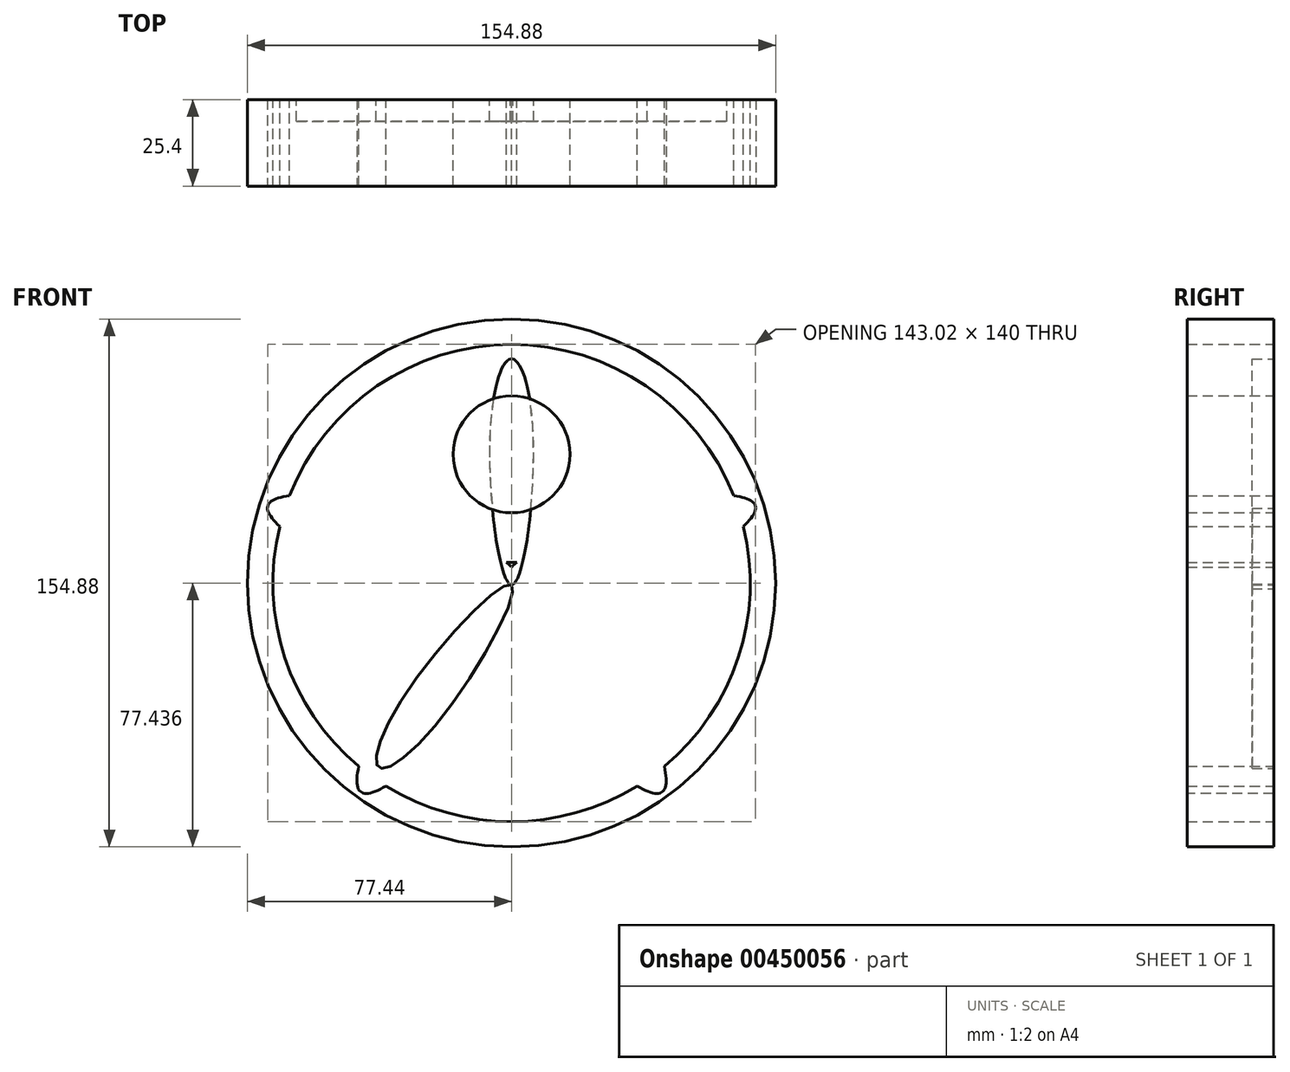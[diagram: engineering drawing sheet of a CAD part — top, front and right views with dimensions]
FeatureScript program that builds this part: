
annotation { "Feature Type Name" : "Feature", "Feature Type Description" : "" }
export const myFeature = defineFeature(function(context is Context, id is Id, definition is map)
    precondition{}
    {
        {
            var Q0;
            Q0=qCreatedBy(makeId("Front.planeOp"),FACE);
            var sketch = newSketch(context, id + "F0", { "sketchPlane" : qUnion([Q0])});
            skCircle(sketch, "E0", {"center": v(0, 0) * mm, "radius": 66.3 * mm, "construction": true});
            skLineSegment(sketch, "E1", {"start": v(0, 0) * mm, "end": v(-63.06, 20.49) * mm, "construction": true});
            skLineSegment(sketch, "E2", {"start": v(-38.97, -53.64) * mm, "end": v(0, 0) * mm, "construction": true});
            skLineSegment(sketch, "E3", {"start": v(0, 0) * mm, "end": v(38.97, -53.64) * mm, "construction": true});
            skLineSegment(sketch, "E4", {"start": v(38.97, -53.64) * mm, "end": v(0, 0) * mm, "construction": true});
            skLineSegment(sketch, "E5", {"start": v(63.06, 20.49) * mm, "end": v(0, 0) * mm, "construction": true});
            skFitSpline(sketch, "E6", {"points": [v(0, 0) * mm, v(-40.37, 19.8) * mm, v(-63.06, 20.49) * mm, v(-44.3, 7.71) * mm, v(0, 0) * mm]});
            skLineSegment(sketch, "E7", {"start": v(-40.37, 19.8) * mm, "end": v(-44.3, 7.71) * mm, "construction": true});
            skSolve(sketch);
        }
        {
            var Q0;
            Q0 = qSketchRegion(id + "F0", true);
            extrude(context, id + "F1", {"entities" : qUnion([Q0]), "depth" : 6.35 * mm});
        }
        {
            var Q0;
            Q0=qCreatedBy(makeId("Right.planeOp"),FACE);
            var sketch = newSketch(context, id + "F2", { "sketchPlane" : qUnion([Q0])});
            skLineSegment(sketch, "E8", {"start": v(0, 0) * mm, "end": v(-63.08, 0) * mm});
            skSolve(sketch);
        }
        {
            var Q0;
            Q0=makeQuery(id+"F1.opExtrude","SWEPT_BODY",BODY,{"disambiguationData":[OSD([sQuery(id+"F0.wireOp",EDGE,"E6")])]});
            var Q1;
            Q1=sQuery(id+"F2.wireOp",EDGE,"E8");
            circularPattern(context, id + "F3", {"entities" : qUnion([Q0]), "axis" : qUnion([Q1]), "angle" : 360 * degree, "instanceCount" : 5, "equalSpace" : true});
        }
        {
            var Q0;
            Q0=qCreatedBy(makeId("Front.planeOp"),FACE);
            var sketch = newSketch(context, id + "F4", { "sketchPlane" : qUnion([Q0])});
            skFitSpline(sketch, "E9.0", {"points": [v(0, 0) * mm, v(1.11, 3.43) * mm, v(-39.76, 23.2) * mm, v(-71.48, 23.22) * mm, v(-45.8, 4.6) * mm, v(-1.11, -3.43) * mm, v(0, 0) * mm]});
            skFitSpline(sketch, "E10.0", {"points": [v(0, 0) * mm, v(-2.92, -2.12) * mm, v(18.53, -42.14) * mm, v(44.18, -60.8) * mm, v(34.35, -30.65) * mm, v(2.92, 2.12) * mm, v(0, 0) * mm]});
            skFitSpline(sketch, "E11.0.0", {"points": [v(0, 0) * mm, v(1.11, -3.43) * mm, v(45.8, 4.6) * mm, v(71.48, 23.22) * mm, v(39.76, 23.2) * mm, v(-1.11, 3.43) * mm, v(0, 0) * mm]});
            skFitSpline(sketch, "E12.trimOffspring", {"points": [v(0, 0) * mm, v(-2.92, 2.12) * mm, v(-34.35, -30.65) * mm, v(-44.18, -60.8) * mm, v(-18.53, -42.14) * mm, v(2.92, -2.12) * mm, v(0, 0) * mm]});
            skPoint(sketch, "E13.visualSharp", {"position": v(0, 0.52) * mm});
            skArc(sketch, "E13.filletArc", {"start": v(-13.78, 9.68) * mm, "mid": v(0, 6.53) * mm, "end": v(13.78, 9.68) * mm});
            skPoint(sketch, "E14.visualSharp", {"position": v(0, -3.68) * mm});
            skArc(sketch, "E14.filletArc", {"start": v(5.59, -16.16) * mm, "mid": v(0, -12.83) * mm, "end": v(-5.59, -16.16) * mm});
            skPoint(sketch, "E15.visualSharp", {"position": v(3.5, -1.14) * mm});
            skArc(sketch, "E15.filletArc", {"start": v(17.1, 0.32) * mm, "mid": v(12.2, -3.96) * mm, "end": v(13.64, -10.3) * mm});
            skPoint(sketch, "E16.visualSharp", {"position": v(-3.5, -1.14) * mm});
            skArc(sketch, "E16.filletArc", {"start": v(-13.64, -10.3) * mm, "mid": v(-12.2, -3.96) * mm, "end": v(-17.1, 0.32) * mm});
            skCircle(sketch, "E17", {"center": v(0, 38.28) * mm, "radius": 17.14 * mm});
            skCircle(sketch, "E18", {"center": v(0, 0.52) * mm, "radius": 70 * mm});
            skCircle(sketch, "E19", {"center": v(0, 0.52) * mm, "radius": 77.44 * mm});
            skSolve(sketch);
        }
        {
            var Q0;
            {var subQ1=sQuery(id+"F4.wireOp",EDGE,"E13.filletArc");Q0=makeQuery(id+"F4.imprint","IMPRINT",FACE,{"disambiguationData":[TD([[makeQuery(id+"F4.imprint","IMPRINT",EDGE,{"derivedFrom":subQ1}),-1.0]])]});}
            var Q1;
            Q1=makeQuery(id+"F4.imprint","IMPRINT",FACE,{"disambiguationData":[TD([[makeQuery(id+"F4.imprint","IMPRINT",EDGE,{"derivedFrom":sQuery(id+"F4.wireOp",EDGE,"E17")}),1.0]])]});
            var Q2;
            Q2=makeQuery(id+"F4.imprint","IMPRINT",FACE,{"disambiguationData":[TD([[makeQuery(id+"F4.imprint","IMPRINT",EDGE,{"derivedFrom":sQuery(id+"F4.wireOp",EDGE,"E18")}),-1.0]])]});
            extrude(context, id + "F5", {"entities" : qUnion([Q0, Q1, Q2]), "depth" : 25.4 * mm});
        }
    });
